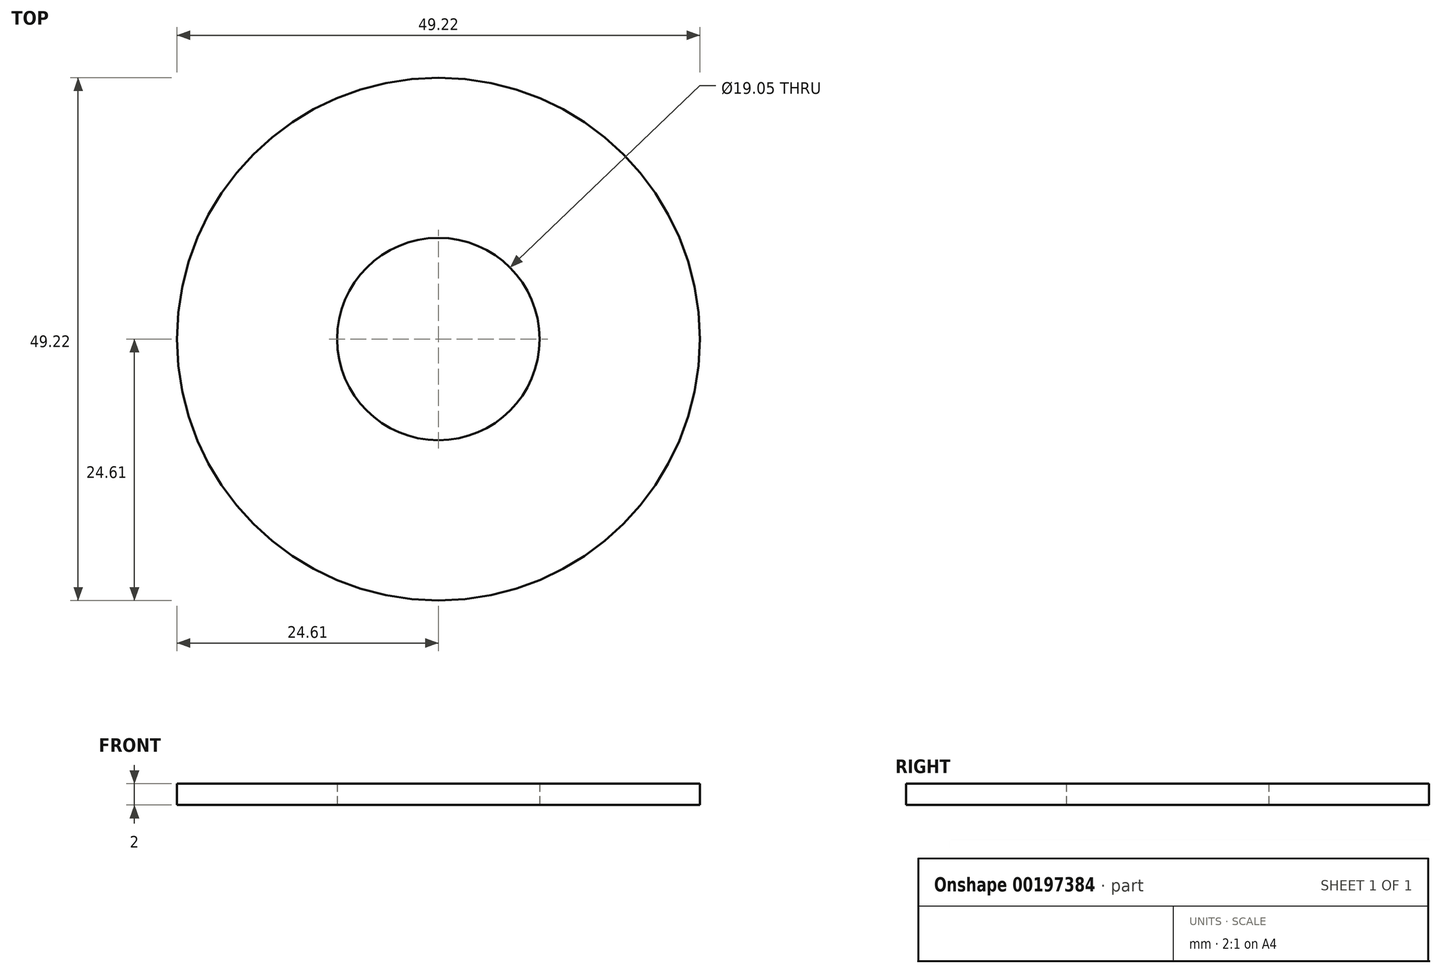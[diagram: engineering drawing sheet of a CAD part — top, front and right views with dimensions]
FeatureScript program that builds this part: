
annotation { "Feature Type Name" : "Feature", "Feature Type Description" : "" }
export const myFeature = defineFeature(function(context is Context, id is Id, definition is map)
    precondition{}
    {
        {
            var Q0;
            Q0=qCreatedBy(makeId("Top.planeOp"),FACE);
            var sketch = newSketch(context, id + "F0", { "sketchPlane" : qUnion([Q0])});
            skCircle(sketch, "E0", {"center": v(0, 0) * mm, "radius": 9.53 * mm});
            skCircle(sketch, "E1", {"center": v(0, 0) * mm, "radius": 24.6 * mm});
            skSolve(sketch);
        }
        {
            var Q0;
            Q0=qSketchRegion(id+"F0",true);
            extrude(context, id + "F1", {"entities" : qUnion([Q0]), "depth" : 2 * mm});
        }
    });
